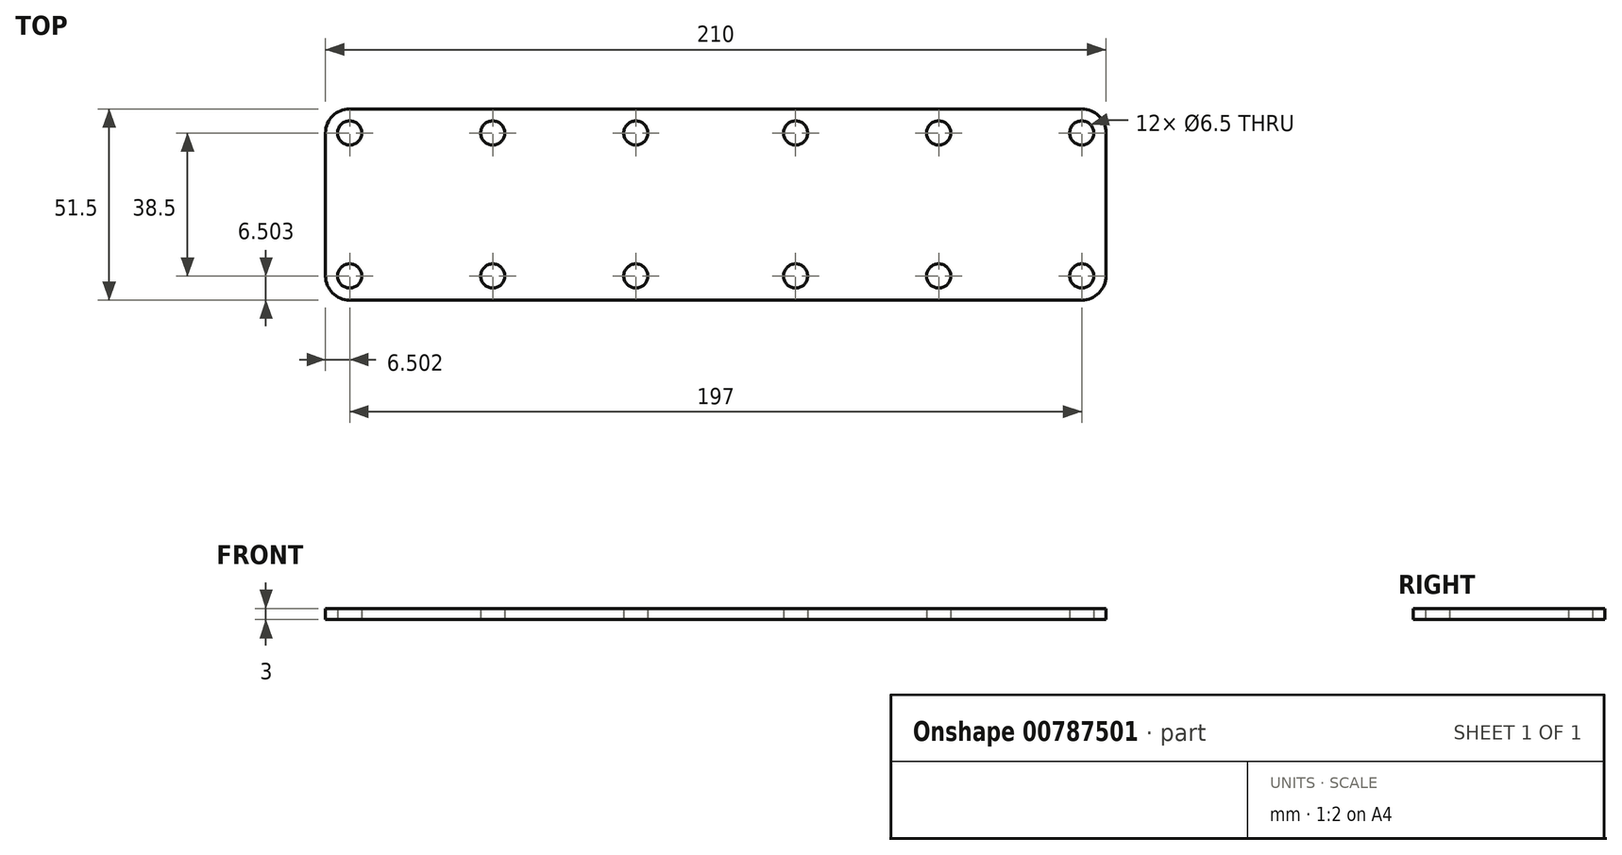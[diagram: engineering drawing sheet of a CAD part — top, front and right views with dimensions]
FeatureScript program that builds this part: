
annotation { "Feature Type Name" : "Feature", "Feature Type Description" : "" }
export const myFeature = defineFeature(function(context is Context, id is Id, definition is map)
    precondition{}
    {
        {
            var Q0;
            Q0=qCreatedBy(makeId("Top.planeOp"),FACE);
            var sketch = newSketch(context, id + "F0", { "sketchPlane" : qUnion([Q0])});
            skLineSegment(sketch, "E0.bottom", {"start": v(-97.02, 8.96) * mm, "end": v(99.98, 8.96) * mm});
            skLineSegment(sketch, "E0.top", {"start": v(-97.02, -42.54) * mm, "end": v(99.98, -42.54) * mm});
            skLineSegment(sketch, "E0.left", {"start": v(-103.52, 2.46) * mm, "end": v(-103.52, -36.04) * mm});
            skLineSegment(sketch, "E0.right", {"start": v(106.48, 2.46) * mm, "end": v(106.48, -36.04) * mm});
            skLineSegment(sketch, "E1.0", {"start": v(-103.52, 2.46) * mm, "end": v(106.48, 2.46) * mm, "construction": true});
            skLineSegment(sketch, "E2.0", {"start": v(99.98, 8.96) * mm, "end": v(99.98, -42.54) * mm, "construction": true});
            skLineSegment(sketch, "E3.0", {"start": v(-97.02, -36.04) * mm, "end": v(106.48, -36.04) * mm, "construction": true});
            skLineSegment(sketch, "E3.1", {"start": v(-97.02, 8.96) * mm, "end": v(-97.02, -36.04) * mm, "construction": true});
            skCircle(sketch, "E4", {"center": v(99.98, 2.46) * mm, "radius": 3.25 * mm});
            skCircle(sketch, "E5", {"center": v(99.98, -36.04) * mm, "radius": 3.25 * mm});
            skLineSegment(sketch, "E6.0", {"start": v(61.48, 8.96) * mm, "end": v(61.48, -42.54) * mm, "construction": true});
            skLineSegment(sketch, "E7.0", {"start": v(22.98, 8.96) * mm, "end": v(22.98, -42.54) * mm, "construction": true});
            skCircle(sketch, "E8", {"center": v(61.48, 2.46) * mm, "radius": 3.25 * mm});
            skCircle(sketch, "E9", {"center": v(22.98, 2.46) * mm, "radius": 3.25 * mm});
            skCircle(sketch, "E10", {"center": v(22.98, -36.04) * mm, "radius": 3.25 * mm});
            skCircle(sketch, "E11", {"center": v(61.48, -36.04) * mm, "radius": 3.25 * mm});
            skLineSegment(sketch, "E12", {"start": v(1.48, 8.96) * mm, "end": v(1.48, -42.54) * mm, "construction": true});
            skCircle(sketch, "E13.MirrorC", {"center": v(-20.02, 2.46) * mm, "radius": 3.25 * mm});
            skCircle(sketch, "E14.MirrorC", {"center": v(-20.02, -36.04) * mm, "radius": 3.25 * mm});
            skCircle(sketch, "E15.MirrorC", {"center": v(-58.52, -36.04) * mm, "radius": 3.25 * mm});
            skCircle(sketch, "E16.MirrorC", {"center": v(-58.52, 2.46) * mm, "radius": 3.25 * mm});
            skCircle(sketch, "E17.MirrorC", {"center": v(-97.02, 2.46) * mm, "radius": 3.25 * mm});
            skCircle(sketch, "E18.MirrorC", {"center": v(-97.02, -36.04) * mm, "radius": 3.25 * mm});
            skPoint(sketch, "E19.visualSharp", {"position": v(-103.52, 8.96) * mm});
            skArc(sketch, "E19.filletArc", {"start": v(-97.02, 8.96) * mm, "mid": v(-101.61, 7.06) * mm, "end": v(-103.52, 2.46) * mm});
            skPoint(sketch, "E20.visualSharp", {"position": v(-103.52, -42.54) * mm});
            skArc(sketch, "E20.filletArc", {"start": v(-103.52, -36.04) * mm, "mid": v(-101.61, -40.63) * mm, "end": v(-97.02, -42.54) * mm});
            skPoint(sketch, "E21.visualSharp", {"position": v(106.48, 8.96) * mm});
            skArc(sketch, "E21.filletArc", {"start": v(106.48, 2.46) * mm, "mid": v(104.58, 7.06) * mm, "end": v(99.98, 8.96) * mm});
            skPoint(sketch, "E22.visualSharp", {"position": v(106.48, -42.54) * mm});
            skArc(sketch, "E22.filletArc", {"start": v(99.98, -42.54) * mm, "mid": v(104.58, -40.63) * mm, "end": v(106.48, -36.04) * mm});
            skSolve(sketch);
        }
        {
            var Q0;
            Q0=makeQuery(id+"F0.imprint","IMPRINT",FACE,{"disambiguationData":[TD([[makeQuery(id+"F0.imprint","IMPRINT",EDGE,{"derivedFrom":sQuery(id+"F0.wireOp",EDGE,"E0.bottom")}),-1.0]])]});
            extrude(context, id + "F1", {"entities" : qUnion([Q0]), "depth" : 3 * mm, "offsetDistance" : 25.4 * mm});
        }
    });
